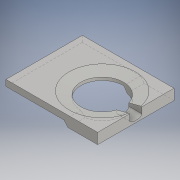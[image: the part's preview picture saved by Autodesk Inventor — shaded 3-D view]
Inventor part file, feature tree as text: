
AUTODESK INVENTOR PART (.ipt)
format: ipt  version: 2016 (Build 200138000, 138)  size: 172,032 bytes
history: native  units: mm
features: sketch x5, extrude x4, projected_geometry x3, revolve x1
ambient origin geometry x8: Origin, YZ Plane, XZ Plane, XY Plane, X Axis, Y Axis, Z Axis, Center Point
bodies: Solid1 (feature_tree)
feature tree (13):
  extrude  "Extrusion1"  Depth=30.0mm
  sketch  "Sketch2"  dims[d2=4.0mm d3=0.0mm d4=4.0mm]
  extrude  "Extrusion2"  Depth=4.0mm
  extrude  "Extrusion3"  Depth=8.726646mm
  extrude  "Extrusion4"  Depth=1.5mm
  revolve  "Revolution2"  [1 undecoded]
  sketch  "Sketch1"  dims[d0=25.0mm d1=30.0mm]
  sketch  "Sketch3"  dims[d5=14.0mm d6=8.726646mm]
  projected_geometry  "Projected Loop1"
  sketch  "Sketch4"  dims[d7=2.0mm d8=1.5mm]
  projected_geometry  "Projected Loop2"
  sketch  "Sketch7"  dims[d9=4.0mm d10=0.0mm d11=10.25mm d12=0.0mm d13=0.5mm d18=15.0deg d19=2.0mm d20=2.0mm d21=90.0deg d26=1.75mm d27=2.0mm d28=2.0mm d29=10.25mm d30=0.0mm]
  projected_geometry  "Projected Loop4"
note: 1 required parameter value undecoded (feature->parameter linkage not recoverable at this tier; creation-order binding heuristic only, values carry confidence <= 0.55)
